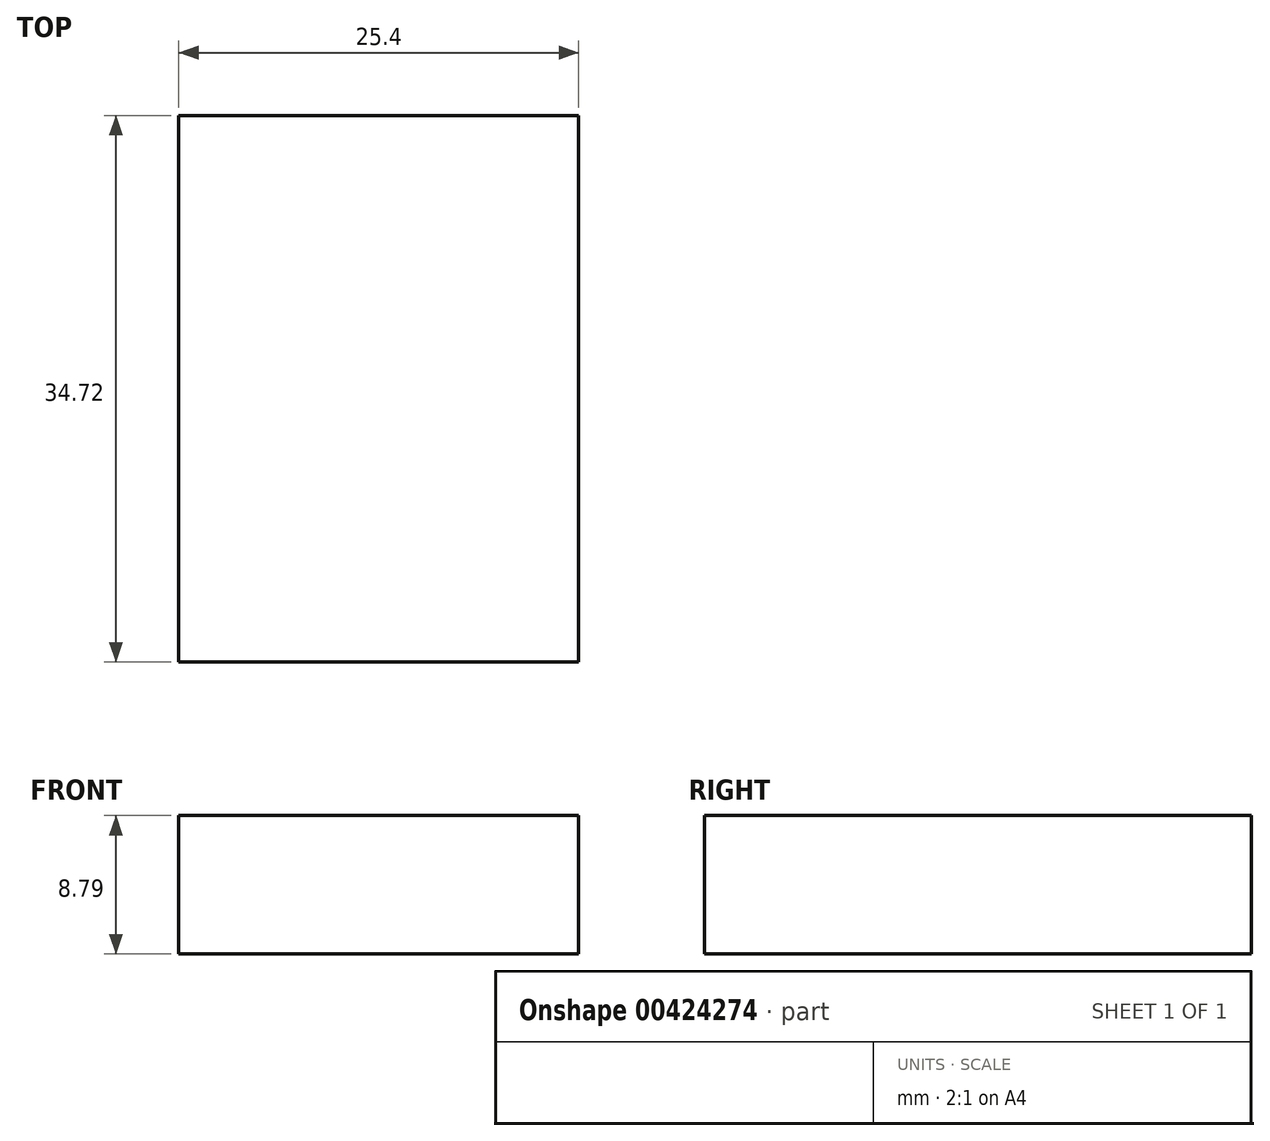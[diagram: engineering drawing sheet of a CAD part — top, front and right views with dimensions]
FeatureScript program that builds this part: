
annotation { "Feature Type Name" : "Feature", "Feature Type Description" : "" }
export const myFeature = defineFeature(function(context is Context, id is Id, definition is map)
    precondition{}
    {
        {
            var Q0;
            Q0=qCreatedBy(makeId("Right.planeOp"),FACE);
            var sketch = newSketch(context, id + "F0", { "sketchPlane" : qUnion([Q0])});
            skLineSegment(sketch, "E0.bottom", {"start": v(-60.87, 39.64) * mm, "end": v(-26.15, 39.64) * mm});
            skLineSegment(sketch, "E0.top", {"start": v(-60.87, 30.85) * mm, "end": v(-26.15, 30.85) * mm});
            skLineSegment(sketch, "E0.left", {"start": v(-60.87, 39.64) * mm, "end": v(-60.87, 30.85) * mm});
            skLineSegment(sketch, "E0.right", {"start": v(-26.15, 39.64) * mm, "end": v(-26.15, 30.85) * mm});
            skSolve(sketch);
        }
        {
            var Q0;
            Q0 = qSketchRegion(id + "F0", true);
            extrude(context, id + "F1", {"entities" : qUnion([Q0]), "depth" : 25.4 * mm});
        }
    });
